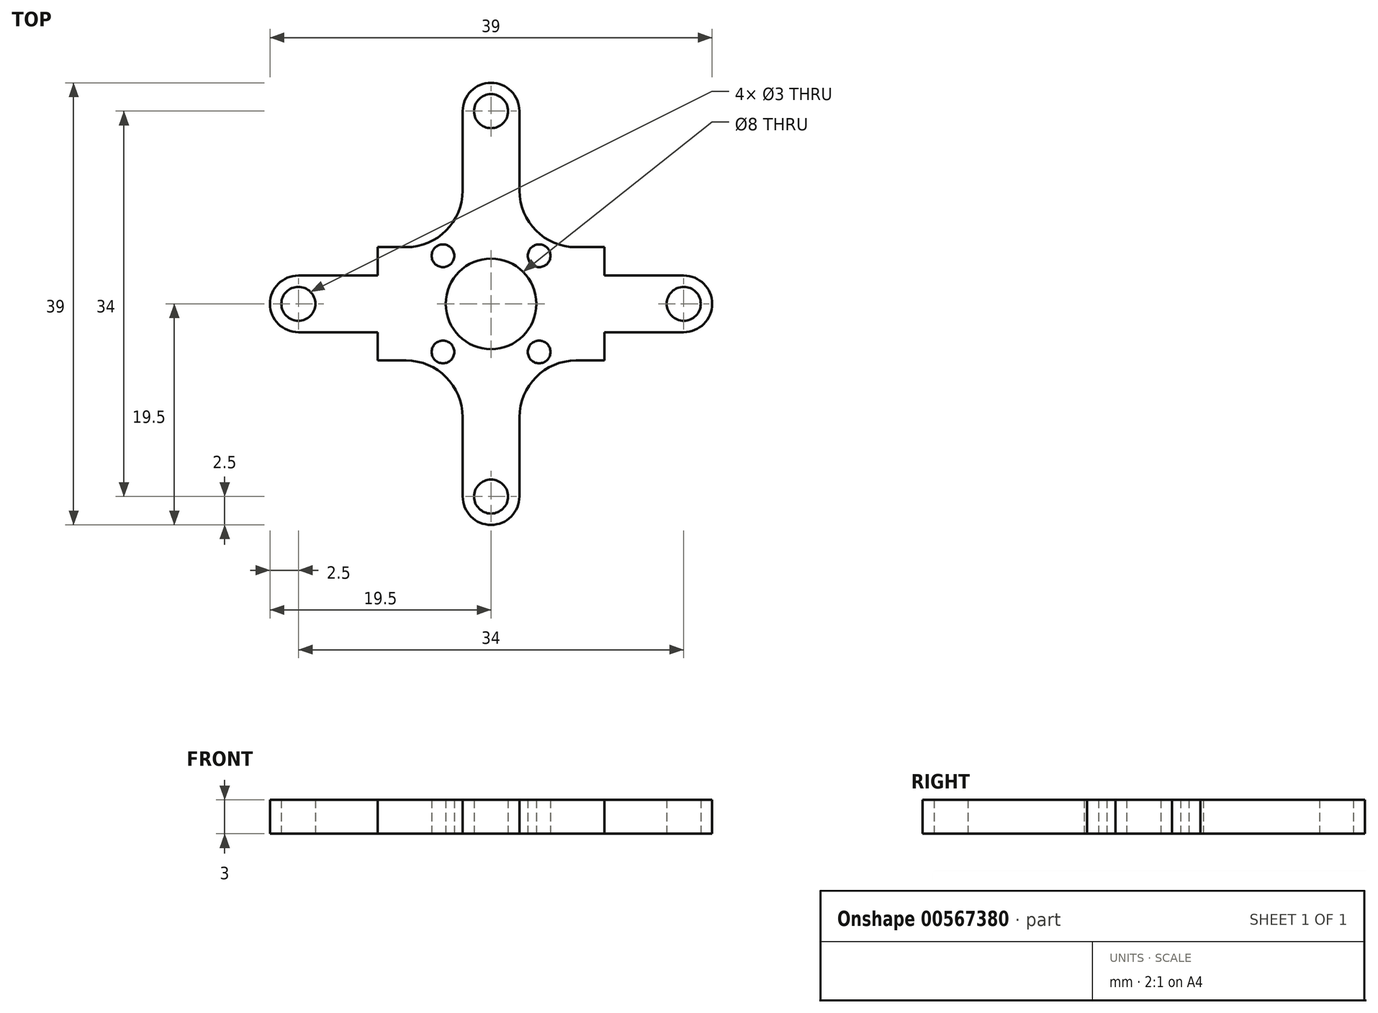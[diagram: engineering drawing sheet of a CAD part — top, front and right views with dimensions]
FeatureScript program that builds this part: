
annotation { "Feature Type Name" : "Feature", "Feature Type Description" : "" }
export const myFeature = defineFeature(function(context is Context, id is Id, definition is map)
    precondition{}
    {
        {
            var Q0;
            Q0=qCreatedBy(makeId("Top.planeOp"),FACE);
            var sketch = newSketch(context, id + "F0", { "sketchPlane" : qUnion([Q0])});
            skLineSegment(sketch, "E0.bottom", {"start": v(-2.5, 17) * mm, "end": v(2.5, 17) * mm});
            skLineSegment(sketch, "E0.top", {"start": v(-2.5, -17) * mm, "end": v(2.5, -17) * mm});
            skLineSegment(sketch, "E0.left", {"start": v(-2.5, 17) * mm, "end": v(-2.5, 10) * mm});
            skLineSegment(sketch, "E0.right", {"start": v(2.5, 17) * mm, "end": v(2.5, 10) * mm});
            skPoint(sketch, "E0.middle", {"position": v(0, 0) * mm});
            skCircle(sketch, "E1", {"center": v(0, 17) * mm, "radius": 2.5 * mm});
            skCircle(sketch, "E2", {"center": v(0, 17) * mm, "radius": 1.5 * mm});
            skCircle(sketch, "E3", {"center": v(0, -17) * mm, "radius": 1.5 * mm});
            skCircle(sketch, "E4", {"center": v(0, -17) * mm, "radius": 2.5 * mm});
            skLineSegment(sketch, "E5.bottom", {"start": v(-10, 5) * mm, "end": v(-7.5, 5) * mm});
            skLineSegment(sketch, "E5.top", {"start": v(-10, -5) * mm, "end": v(-7.5, -5) * mm});
            skLineSegment(sketch, "E5.left", {"start": v(-10, 5) * mm, "end": v(-10, -5) * mm});
            skLineSegment(sketch, "E5.right", {"start": v(10, 5) * mm, "end": v(10, -5) * mm});
            skLineSegment(sketch, "E6.bottom", {"start": v(17, -2.5) * mm, "end": v(-17, -2.5) * mm});
            skLineSegment(sketch, "E6.top", {"start": v(17, 2.5) * mm, "end": v(-17, 2.5) * mm});
            skLineSegment(sketch, "E6.left", {"start": v(17, -2.5) * mm, "end": v(17, 2.5) * mm});
            skLineSegment(sketch, "E6.right", {"start": v(-17, -2.5) * mm, "end": v(-17, 2.5) * mm});
            skCircle(sketch, "E7", {"center": v(-17, 0) * mm, "radius": 1.5 * mm});
            skCircle(sketch, "E8", {"center": v(-17, 0) * mm, "radius": 2.5 * mm});
            skCircle(sketch, "E9", {"center": v(17, 0) * mm, "radius": 2.5 * mm});
            skCircle(sketch, "E10", {"center": v(17, 0) * mm, "radius": 1.5 * mm});
            skCircle(sketch, "E11", {"center": v(0, 0) * mm, "radius": 4 * mm});
            skCircle(sketch, "E12", {"center": v(-4.24, 4.24) * mm, "radius": 1 * mm});
            skLineSegment(sketch, "E13", {"start": v(-4.24, 4.24) * mm, "end": v(0, 0) * mm});
            skCircle(sketch, "E14.1.0", {"center": v(-4.24, -4.24) * mm, "radius": 1 * mm});
            skCircle(sketch, "E14.2.0", {"center": v(4.24, -4.24) * mm, "radius": 1 * mm});
            skCircle(sketch, "E14.3.0", {"center": v(4.24, 4.24) * mm, "radius": 1 * mm});
            skLineSegment(sketch, "E15.trimOffspring", {"start": v(7.5, 5) * mm, "end": v(10, 5) * mm});
            skLineSegment(sketch, "E16.trimOffspring", {"start": v(7.5, -5) * mm, "end": v(10, -5) * mm});
            skLineSegment(sketch, "E17.trimOffspring", {"start": v(2.5, 3.12) * mm, "end": v(2.5, -3.12) * mm});
            skLineSegment(sketch, "E18.trimOffspring", {"start": v(-2.5, 3.12) * mm, "end": v(-2.5, -3.12) * mm});
            skLineSegment(sketch, "E19.trimOffspring", {"start": v(-2.5, -10) * mm, "end": v(-2.5, -17) * mm});
            skLineSegment(sketch, "E20.trimOffspring", {"start": v(2.5, -10) * mm, "end": v(2.5, -17) * mm});
            skPoint(sketch, "E21.visualSharp", {"position": v(-2.5, -5) * mm});
            skArc(sketch, "E21.filletArc", {"start": v(-2.5, -10) * mm, "mid": v(-3.96, -6.46) * mm, "end": v(-7.5, -5) * mm});
            skPoint(sketch, "E22.visualSharp", {"position": v(2.5, -5) * mm});
            skArc(sketch, "E22.filletArc", {"start": v(7.5, -5) * mm, "mid": v(3.96, -6.46) * mm, "end": v(2.5, -10) * mm});
            skPoint(sketch, "E23.visualSharp", {"position": v(2.5, 5) * mm});
            skArc(sketch, "E23.filletArc", {"start": v(2.5, 10) * mm, "mid": v(3.96, 6.46) * mm, "end": v(7.5, 5) * mm});
            skPoint(sketch, "E24.visualSharp", {"position": v(-2.5, 5) * mm});
            skArc(sketch, "E24.filletArc", {"start": v(-7.5, 5) * mm, "mid": v(-3.96, 6.46) * mm, "end": v(-2.5, 10) * mm});
            skSolve(sketch);
        }
        {
            var Q0;
            Q0=qSketchRegion(id+"F0",true);
            extrude(context, id + "F1", {"entities" : qUnion([Q0]), "depth" : 3 * mm, "offsetDistance" : 25 * mm});
        }
    });
